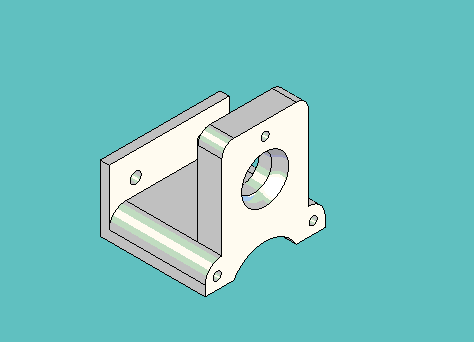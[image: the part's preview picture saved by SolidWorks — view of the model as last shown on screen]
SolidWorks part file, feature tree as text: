
SOLIDWORKS PART (.sldprt)
format: sldprt  version: not decoded by parser v0  size: 554,496 bytes
history: native  units: mm
features: sketch x8, extrude x3, cut_extrude x3, fillet x2, material x1, revolve x1, boolean_combine x1 (+11 scaffold rows collapsed)
feature tree (30):
  scaffold x11  (default folders/planes/origin — collapsed)
  material  "Material <not specified>"
  sketch  "Sketch1"  dims[D1=~2.38125mm D2=~2.38125mm D3=6.35mm D4=11.1125mm D5=15.875mm D6=25.4mm]
  sketch  "Sketch6"  dims[c1.D3=9.525mm c1.D5=19.05mm c1.D1=22.86mm c1.D2=11.1125mm c1.D4=31.75mm c2.D2=12.7mm c2.D3=11.43mm c2.D5=22.86mm c2.D6=4.7625mm]
  extrude  "Extrude3"  Depth=2.38125mm
  sketch  "Sketch7"  dims[D1=~2.38125mm]
  extrude  "Extrude4"  Depth=25.4mm
  sketch  "Sketch2"  dims[c1.D2=12.7mm c1.D3=9.525mm c1.D4=9.525mm c1.D5=6.985mm c1.D1=25.4mm c2.D3=12.7mm c2.D4=22.86mm c2.D1=0.0mm]
  extrude  "Extrude5"  Depth=6.35mm
  sketch  "Sketch4"  dims[D1=2.9464mm D2=2.9464mm D3=8.89mm D4=6.35mm]
  cut_extrude  "Cut-Extrude3"  [1 undecoded]
  fillet  "Fillet3"  Radius=4.445mm
  fillet  "Fillet4"  Radius=3.175mm
  sketch  "Sketch10"  dims[c1.D1=2.159mm c1.D2=~4.129367mm c1.D4=2.159mm c2.D2=1.5875mm c2.D3=12.7mm c2.D5=24.13mm]
  cut_extrude  "Cut-Extrude4"  Depth=9.525mm
  sketch  "Sketch11"  dims[c1.D3=12.7mm c1.D1=14.2875mm c1.D2=~28.971875mm c2.D1=14.2875mm c2.D2=~28.971875mm]
  revolve  "Revolve2"  Angle=360deg
  boolean_combine  "Combine1"
  sketch  "Sketch12"  dims[D1=9.525mm]
  cut_extrude  "Cut-Extrude5"  [1 undecoded]
decode coverage: 15 of 18 modeling features carry decoded parameters
note: ~ marks probable driven/reference dimensions
note: 2 parameter values undecoded
note: suppression state not decoded; provenance and decode notes live in map.json
